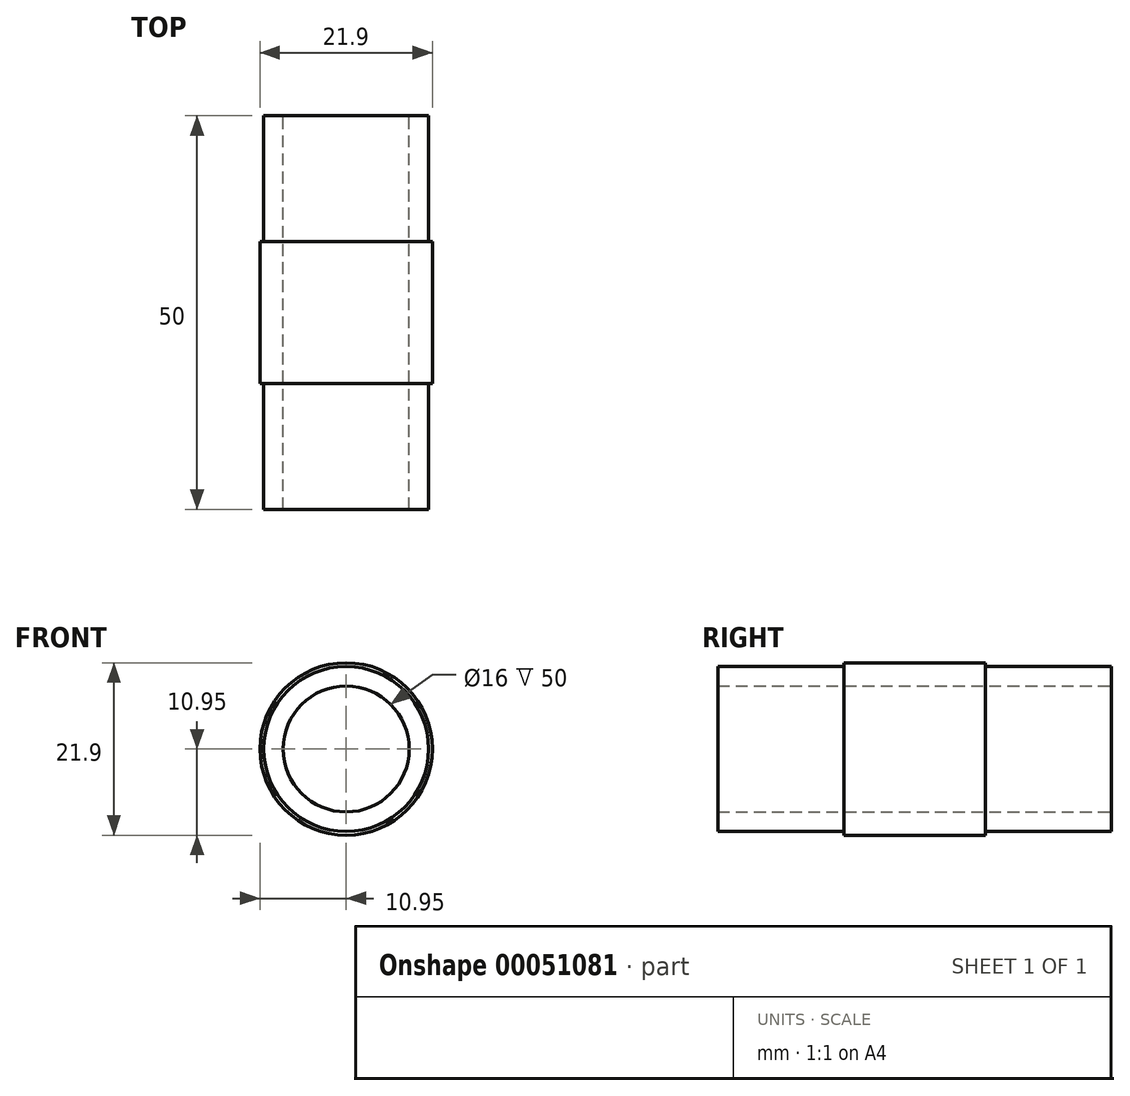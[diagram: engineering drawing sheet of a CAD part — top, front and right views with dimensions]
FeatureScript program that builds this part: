
annotation { "Feature Type Name" : "Feature", "Feature Type Description" : "" }
export const myFeature = defineFeature(function(context is Context, id is Id, definition is map)
    precondition{}
    {
        {
            var Q0;
            Q0=qCreatedBy(makeId("Front.planeOp"),FACE);
            var sketch = newSketch(context, id + "F0", { "sketchPlane" : qUnion([Q0])});
            skCircle(sketch, "E0", {"center": v(0, 0) * mm, "radius": 10.48 * mm});
            skCircle(sketch, "E1", {"center": v(0, 0) * mm, "radius": 8 * mm});
            skSolve(sketch);
        }
        {
            var Q0;
            Q0=qSketchRegion(id+"F0",true);
            extrude(context, id + "F1", {"entities" : qUnion([Q0]), "depth" : 16 * mm});
        }
        {
            var Q0;
            Q0=qCreatedBy(makeId("Front.planeOp"),FACE);
            var sketch = newSketch(context, id + "F2", { "sketchPlane" : qUnion([Q0])});
            skCircle(sketch, "E2", {"center": v(0, 0) * mm, "radius": 8 * mm});
            skCircle(sketch, "E3", {"center": v(0, 0) * mm, "radius": 10.95 * mm});
            skSolve(sketch);
        }
        {
            var Q0;
            Q0=qSketchRegion(id+"F2",true);
            extrude(context, id + "F3", {"entities" : qUnion([Q0]), "operationType" : NewBodyOperationType.ADD, "oppositeDirection" : true, "depth" : (50 - (16 + 16)) * mm});
        }
        {
            var Q0;
            Q0=makeQuery(id+"F3.opExtrude","CAP_FACE",FACE,{"disambiguationData":[OSD([sQuery(id+"F2.wireOp",EDGE,"E2"),sQuery(id+"F2.wireOp",EDGE,"E3")])],"isStart":false});
            var sketch = newSketch(context, id + "F4", { "sketchPlane" : qUnion([Q0])});
            skCircle(sketch, "E4", {"center": v(0, 0) * mm, "radius": 10.48 * mm});
            skCircle(sketch, "E5", {"center": v(0, 0) * mm, "radius": 8 * mm});
            skSolve(sketch);
        }
        {
            var Q0;
            Q0=qSketchRegion(id+"F4",true);
            extrude(context, id + "F5", {"entities" : qUnion([Q0]), "operationType" : NewBodyOperationType.ADD, "depth" : 16 * mm});
        }
    });
